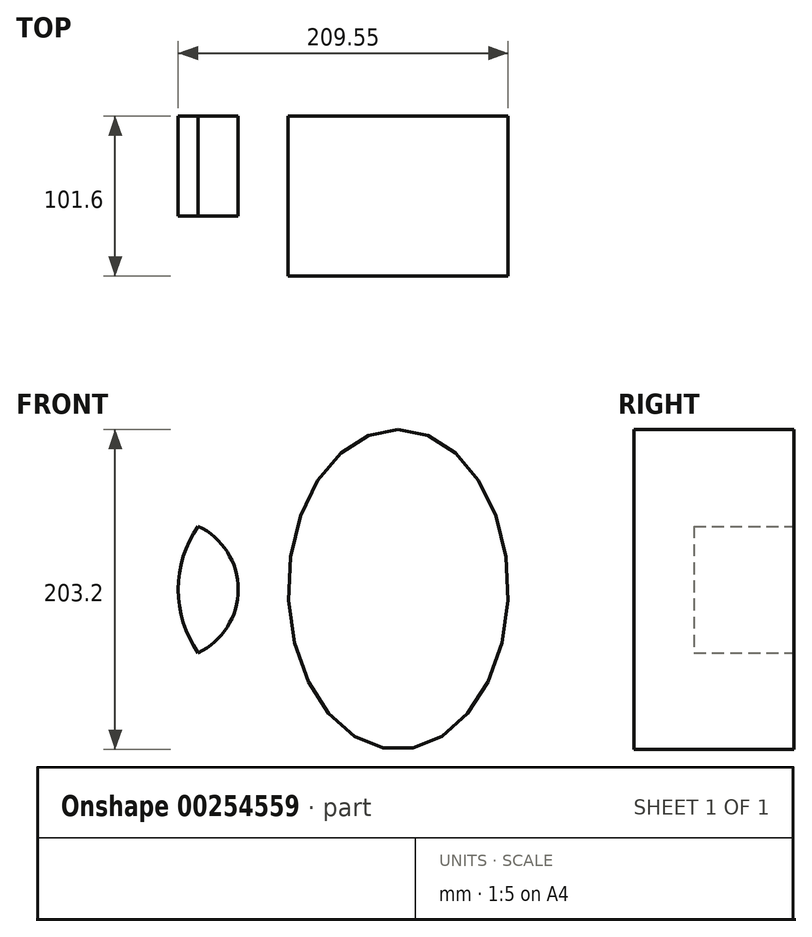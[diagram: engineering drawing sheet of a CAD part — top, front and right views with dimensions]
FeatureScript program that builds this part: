
annotation { "Feature Type Name" : "Feature", "Feature Type Description" : "" }
export const myFeature = defineFeature(function(context is Context, id is Id, definition is map)
    precondition{}
    {
        {
            var Q0;
            Q0=qCreatedBy(makeId("Front.planeOp"),FACE);
            var sketch = newSketch(context, id + "F0", { "sketchPlane" : qUnion([Q0])});
            skLineSegment(sketch, "E0", {"start": v(-76.2, 0) * mm, "end": v(0, 0) * mm});
            skCircle(sketch, "E1", {"center": v(-76.2, 0) * mm, "radius": 44.45 * mm});
            skCircle(sketch, "E2", {"center": v(0, 0) * mm, "radius": 69.85 * mm});
            skLineSegment(sketch, "E3", {"start": v(-69.85, 0) * mm, "end": v(-31.75, 0) * mm});
            skLineSegment(sketch, "E4", {"start": v(69.85, 0) * mm, "end": v(69.85, 101.6) * mm});
            skEllipse(sketch, "E5", {"center": v(69.85, 0) * mm, "majorRadius": 101.6 * mm, "minorRadius": 69.85 * mm, "majorAxis": v(0, 1)});
            skSolve(sketch);
        }
        {
            var Q0;
            {var subQ0=sQuery(id+"F0.wireOp",EDGE,"E2");var subQ1=sQuery(id+"F0.wireOp",EDGE,"E1");var subQ2=makeQuery(id+"F0.imprint","INTERSECT",VERTEX,{"disambiguationData":[OD(0.0)],"derivedFrom":[subQ1,subQ0]});Q0=makeQuery(id+"F0.imprint","IMPRINT",FACE,{"disambiguationData":[TD([[makeQuery(id+"F0.imprint","IMPRINT",EDGE,{"disambiguationData":[TD([[subQ2,-1.0]])],"derivedFrom":subQ1}),1.0]])]});}
            extrude(context, id + "F1", {"entities" : qUnion([Q0]), "depth" : 25.4 * mm});
        }
        {
            var Q0;
            {var subQ0=sQuery(id+"F0.wireOp",EDGE,"E3");Q0=makeQuery(id+"F0.imprint","IMPRINT",FACE,{"disambiguationData":[TD([[makeQuery(id+"F0.imprint","IMPRINT",EDGE,{"derivedFrom":subQ0}),1.0]])]});}
            var Q1;
            {var subQ0=sQuery(id+"F0.wireOp",EDGE,"E3");Q1=makeQuery(id+"F0.imprint","IMPRINT",FACE,{"disambiguationData":[TD([[makeQuery(id+"F0.imprint","IMPRINT",EDGE,{"derivedFrom":subQ0}),-1.0]])]});}
            var Q2;
            {var subQ3=sQuery(id+"F0.wireOp",EDGE,"E1");var subQ5=sQuery(id+"F0.wireOp",EDGE,"E2");var subQ6=makeQuery(id+"F0.imprint","INTERSECT",VERTEX,{"disambiguationData":[OD(1.0)],"derivedFrom":[subQ3,subQ5]});Q2=makeQuery(id+"F0.imprint","IMPRINT",FACE,{"disambiguationData":[TD([[makeQuery(id+"F0.imprint","IMPRINT",EDGE,{"disambiguationData":[TD([[subQ6,-1.0]])],"derivedFrom":subQ5}),1.0]])]});}
            var Q3;
            {var subQ3=sQuery(id+"F0.wireOp",EDGE,"E1");var subQ5=sQuery(id+"F0.wireOp",EDGE,"E2");var subQ6=makeQuery(id+"F0.imprint","INTERSECT",VERTEX,{"disambiguationData":[OD(0.0)],"derivedFrom":[subQ3,subQ5]});Q3=makeQuery(id+"F0.imprint","IMPRINT",FACE,{"disambiguationData":[TD([[makeQuery(id+"F0.imprint","IMPRINT",EDGE,{"disambiguationData":[TD([[subQ6,1.0]])],"derivedFrom":subQ5}),1.0]])]});}
            extrude(context, id + "F2", {"entities" : qUnion([Q0, Q1, Q2, Q3]), "operationType" : NewBodyOperationType.ADD, "depth" : 63.5 * mm});
        }
        {
            var Q0;
            {var subQ0=sQuery(id+"F0.wireOp",EDGE,"E2");var subQ1=makeQuery(id+"F0.imprint","INTERSECT",VERTEX,{"derivedFrom":[subQ0,sQuery(id+"F0.wireOp",EDGE,"E4")]});Q0=makeQuery(id+"F0.imprint","IMPRINT",FACE,{"disambiguationData":[TD([[makeQuery(id+"F0.imprint","IMPRINT",EDGE,{"disambiguationData":[TD([[subQ1,-1.0]])],"derivedFrom":subQ0}),1.0]])]});}
            var Q1;
            {var subQ0=sQuery(id+"F0.wireOp",EDGE,"E4");Q1=makeQuery(id+"F0.imprint","IMPRINT",FACE,{"disambiguationData":[TD([[makeQuery(id+"F0.imprint","IMPRINT",EDGE,{"derivedFrom":subQ0}),1.0]])]});}
            var Q2;
            {var subQ0=sQuery(id+"F0.wireOp",EDGE,"E4");Q2=makeQuery(id+"F0.imprint","IMPRINT",FACE,{"disambiguationData":[TD([[makeQuery(id+"F0.imprint","IMPRINT",EDGE,{"derivedFrom":subQ0}),-1.0]])]});}
            extrude(context, id + "F3", {"entities" : qUnion([Q0, Q1, Q2]), "operationType" : NewBodyOperationType.ADD, "depth" : 101.6 * mm});
        }
    });
